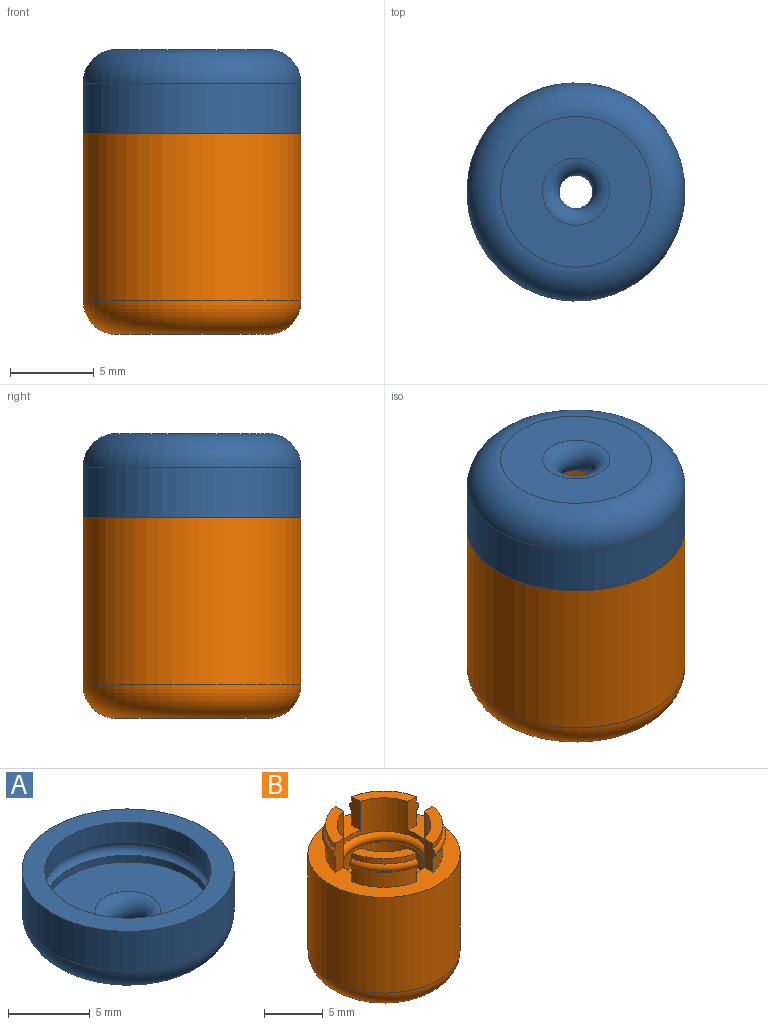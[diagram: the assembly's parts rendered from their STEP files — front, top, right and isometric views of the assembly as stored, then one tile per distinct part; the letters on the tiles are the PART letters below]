
ASSEMBLY  parts=2 mates=1
PART A: 9 faces, bbox 14.1x14.1x5 mm
  f0: cylinder r=5.1mm len=10.2mm, axis (0,0,-1), area 16.3mm2, adj f2,f8
  f1: plane 9x9mm, normal (0,0,-1), area 51.1mm2, adj f6,f7
  f2: plane 10.2x10.2mm, normal (0,0,1), area 69.1mm2, adj f0,f6
  f3: cylinder r=5.1mm len=10.2mm, axis (0,0,-1), area 48.4mm2, adj f4,f8
  f4: plane 13x13mm, normal (0,0,1), area 51mm2, adj f3,f5
  f5: cylinder r=6.5mm len=13mm, axis (0,0,-1), area 122.5mm2, adj f4,f7
  f6: torus R=2mm, axis (0,0,1), area 26.9mm2, adj f1,f2
  f7: torus R=4.5mm, axis (0,0,-1), area 114mm2, adj f1,f5
  f8: torus R=5mm, axis (0,0,-1), area 46.1mm2, adj f0,f3
PART B: 37 faces, bbox 14.1x14.1x15 mm
  f0: cylinder r=5mm len=3.9mm, axis (0,0,-1), area 9.2mm2, adj f10,f24,f29,f35
  f1: cylinder r=5mm len=3.9mm, axis (0,0,-1), area 9.2mm2, adj f11,f24,f34,f36
  f2: cylinder r=5mm len=3.9mm, axis (0,0,-1), area 9.2mm2, adj f12,f24,f32,f33
  f3: cylinder r=5mm len=3.9mm, axis (0,0,-1), area 3.3mm2, adj f6,f10,f29,f35
  f4: cylinder r=5mm len=3.9mm, axis (0,0,-1), area 3.3mm2, adj f7,f11,f34,f36
  f5: cylinder r=5mm len=3.9mm, axis (0,0,-1), area 3.3mm2, adj f8,f12,f32,f33
  f6: plane 3.9x3.9mm, normal (0,0,1), area 5.1mm2, adj f3,f9,f29,f35
  f7: plane 3.9x3.9mm, normal (0,0,1), area 5.1mm2, adj f4,f9,f34,f36
  f8: plane 3.9x3.9mm, normal (0,0,1), area 5.1mm2, adj f5,f9,f32,f33
  f9: cylinder r=4mm len=8mm, axis (0,0,1), area 63.7mm2, adj f6,f7,f8,f18,f21,f24,f29,f30
  f10: torus R=4.75mm, axis (0,0,-1), area 6.4mm2, adj f0,f3,f29,f35
  f11: torus R=4.75mm, axis (0,0,-1), area 6.4mm2, adj f1,f4,f34,f36
  f12: torus R=4.75mm, axis (0,0,-1), area 6.4mm2, adj f2,f5,f32,f33
  f13: cylinder r=4mm len=8mm, axis (0,0,1), area 12.6mm2, adj f23,f27
  f14: cylinder r=4mm len=8mm, axis (0,0,1), area 50.3mm2, adj f22,f23
  f15: cylinder r=4mm len=8mm, axis (0,0,1), area 50.3mm2, adj f21,f22
  f16: cylinder r=5mm len=3.9mm, axis (0,0,-1), area 9.2mm2, adj f20,f24,f30,f31
  f17: cylinder r=5mm len=3.9mm, axis (0,0,-1), area 3.3mm2, adj f18,f20,f30,f31
  f18: plane 3.9x3.9mm, normal (0,0,1), area 5.1mm2, adj f9,f17,f30,f31
  f19: plane 9x9mm, normal (0,0,-1), area 51.1mm2, adj f26,f28
  f20: torus R=4.75mm, axis (0,0,-1), area 6.4mm2, adj f16,f17,f30,f31
  f21: torus R=4mm, axis (0,0,-1), area 36.3mm2, adj f9,f15
  f22: torus R=4mm, axis (0,0,-1), area 36.3mm2, adj f14,f15
  f23: torus R=4mm, axis (0,0,-1), area 36.3mm2, adj f13,f14
  f24: plane 13x13mm, normal (0,0,1), area 62.3mm2, adj f0,f1,f2,f9,f16,f25,f29,f30
  f25: cylinder r=6.5mm len=13mm, axis (0,0,-1), area 408.4mm2, adj f24,f26
  f26: torus R=4.5mm, axis (0,0,1), area 114mm2, adj f19,f25
  f27: torus R=2mm, axis (0,0,1), area 64.6mm2, adj f13,f28
  f28: torus R=2mm, axis (0,0,1), area 26.9mm2, adj f19,f27
  f29: plane 3x1.28mm, normal (-1,0,0), area 3.2mm2, adj f0,f3,f6,f9,f10,f24
  f30: plane 3x1.28mm, normal (1,0,0), area 3.2mm2, adj f9,f16,f17,f18,f20,f24
  f31: plane 3x1.28mm, normal (0,1,0), area 3.2mm2, adj f9,f16,f17,f18,f20,f24
  f32: plane 3x1.28mm, normal (0,-1,0), area 3.2mm2, adj f2,f5,f8,f9,f12,f24
  f33: plane 3x1.28mm, normal (1,0,0), area 3.2mm2, adj f2,f5,f8,f9,f12,f24
  f34: plane 3x1.28mm, normal (-1,0,0), area 3.2mm2, adj f1,f4,f7,f9,f11,f24
  f35: plane 3x1.28mm, normal (0,1,0), area 3.2mm2, adj f0,f3,f6,f9,f10,f24
  f36: plane 3x1.28mm, normal (0,-1,0), area 3.2mm2, adj f1,f4,f7,f9,f11,f24
PLACE A rot(axis=(0.71,0.71,0),180deg) t=(0,0,17)mm
PLACE B at identity
MATE fastened A.f0 <-> B.f9  axis (0,0,-1) through (0,0,12)mm
